annotation { "Feature Type Name" : "Feature", "Feature Type Description" : "" }
export const myFeature = defineFeature(function(context is Context, id is Id, definition is map)
    precondition{}
    {
        {
            var Q0;
            Q0=qCreatedBy(makeId("Front.planeOp"),FACE);
            var sketch = newSketch(context, id + "F0", { "sketchPlane" : qUnion([Q0])});
            skText(sketch, "E0", { "text": "Graces Medals", "fontName": "OpenSans-Bold.ttf"});
            const initialGuessF0  = {"E0": [-0.01396, 0.003, 1, 0, 0.00646]};
            skSetInitialGuess(sketch, initialGuessF0);
            skSolve(sketch);
        }
        {
            var Q0;
            Q0 = qSketchRegion(id + "F0", true);
            extrude(context, id + "F1", {"entities" : qUnion([Q0]), "depth" : 3 * mm, "offsetDistance" : 25 * mm});
        }
        {
            var Q0;
            Q0=qCreatedBy(makeId("Front.planeOp"),FACE);
            var sketch = newSketch(context, id + "F2", { "sketchPlane" : qUnion([Q0])});
            skLineSegment(sketch, "E1.bottom", {"start": v(-11.2, 3.33) * mm, "end": v(49.8, 3.33) * mm});
            skLineSegment(sketch, "E1.top", {"start": v(-11.2, 2.13) * mm, "end": v(49.8, 2.13) * mm});
            skLineSegment(sketch, "E1.left", {"start": v(-11.2, 3.33) * mm, "end": v(-11.2, 2.13) * mm});
            skLineSegment(sketch, "E1.right", {"start": v(49.8, 3.33) * mm, "end": v(49.8, 2.13) * mm});
            skSolve(sketch);
        }
        {
            var Q0;
            Q0 = qSketchRegion(id + "F2", true);
            extrude(context, id + "F3", {"entities" : qUnion([Q0]), "depth" : 4 * mm, "offsetDistance" : 25 * mm});
        }
        {
            var Q0;
            Q0=qCreatedBy(makeId("Front.planeOp"),FACE);
            var sketch = newSketch(context, id + "F4", { "sketchPlane" : qUnion([Q0])});
            skText(sketch, "E2", { "text": "Emmas Medals", "fontName": "OpenSans-Bold.ttf"});
            const initialGuessF4  = {"E2": [-0.00699, -0.01044, 1, 0, 0.00673]};
            skSetInitialGuess(sketch, initialGuessF4);
            skSolve(sketch);
        }
        {
            var Q0;
            Q0 = qSketchRegion(id + "F4", true);
            extrude(context, id + "F5", {"entities" : qUnion([Q0]), "depth" : 3 * mm, "offsetDistance" : 25 * mm});
        }
        {
            var Q0;
            Q0=qCreatedBy(makeId("Front.planeOp"),FACE);
            var sketch = newSketch(context, id + "F6", { "sketchPlane" : qUnion([Q0])});
            skLineSegment(sketch, "E3.bottom", {"start": v(-5.65, -9.96) * mm, "end": v(61.02, -9.96) * mm});
            skLineSegment(sketch, "E3.top", {"start": v(-5.65, -11.3) * mm, "end": v(61.02, -11.3) * mm});
            skLineSegment(sketch, "E3.left", {"start": v(-5.65, -9.96) * mm, "end": v(-5.65, -11.3) * mm});
            skLineSegment(sketch, "E3.right", {"start": v(61.02, -9.96) * mm, "end": v(61.02, -11.3) * mm});
            skSolve(sketch);
        }
        {
            var Q0;
            Q0 = qSketchRegion(id + "F6", true);
            extrude(context, id + "F7", {"entities" : qUnion([Q0]), "depth" : 4 * mm, "offsetDistance" : 25 * mm});
        }
        {
            var Q0;
            Q0=qCreatedBy(makeId("Front.planeOp"),FACE);
            var sketch = newSketch(context, id + "F8", { "sketchPlane" : qUnion([Q0])});
            skText(sketch, "E4", { "text": "S", "fontName": "OpenSans-Bold.ttf"});
            skText(sketch, "E5", { "text": "S", "fontName": "OpenSans-Bold.ttf"});
            const initialGuessF8  = {"E4": [-0.04804, 0.0456, 1, 0, 0.03], "E5": [0.01477, 0.04587, 1, 0, 0.02896]};
            skSetInitialGuess(sketch, initialGuessF8);
            skSolve(sketch);
        }
        {
            var Q0;
            Q0=qCreatedBy(makeId("Front.planeOp"),FACE);
            var sketch = newSketch(context, id + "F9", { "sketchPlane" : qUnion([Q0])});
            skText(sketch, "E6", { "text": "UPER", "fontName": "OpenSans-Bold.ttf"});
            const initialGuessF9  = {"E6": [-0.03335, 0.05668, 1, 0, 0.01108]};
            skSetInitialGuess(sketch, initialGuessF9);
            skSolve(sketch);
        }
        {
            var Q0;
            Q0=qCreatedBy(makeId("Front.planeOp"),FACE);
            var sketch = newSketch(context, id + "F10", { "sketchPlane" : qUnion([Q0])});
            skText(sketch, "E7", { "text": "TAR", "fontName": "OpenSans-Bold.ttf"});
            const initialGuessF10  = {"E7": [0.03342, 0.04587, 1, 0, 0.01102]};
            skSetInitialGuess(sketch, initialGuessF10);
            skSolve(sketch);
        }
        {
            var Q0;
            Q0 = qSketchRegion(id + "F10", true);
            var Q1;
            Q1 = qSketchRegion(id + "F9", true);
            var Q2;
            Q2=makeQuery(id+"F8.imprint","IMPRINT",FACE,{"disambiguationData":[TD([[makeQuery(id+"F8.imprint","IMPRINT",EDGE,{"derivedFrom":sQuery(id+"F8.wireOp",EDGE,"E4.sketch_text.stroke-0")}),-1.0]])]});
            var Q3;
            Q3=makeQuery(id+"F8.imprint","IMPRINT",FACE,{"disambiguationData":[TD([[makeQuery(id+"F8.imprint","IMPRINT",EDGE,{"derivedFrom":sQuery(id+"F8.wireOp",EDGE,"E5.sketch_text.stroke-0")}),-1.0]])]});
            extrude(context, id + "F11", {"entities" : qUnion([Q0, Q1, Q2, Q3]), "depth" : 7 * mm, "offsetDistance" : 25 * mm});
        }
        {
            var Q0;
            Q0=makeQuery(id+"F11.opExtrude","SWEPT_BODY",BODY,{"disambiguationData":[OSD([sQuery(id+"F9.wireOp",EDGE,"E6.sketch_text.stroke-15"),sQuery(id+"F9.wireOp",EDGE,"E6.sketch_text.stroke-16"),sQuery(id+"F9.wireOp",EDGE,"E6.sketch_text.stroke-17"),sQuery(id+"F9.wireOp",EDGE,"E6.sketch_text.stroke-18"),sQuery(id+"F9.wireOp",EDGE,"E6.sketch_text.stroke-19"),sQuery(id+"F9.wireOp",EDGE,"E6.sketch_text.stroke-20"),sQuery(id+"F9.wireOp",EDGE,"E6.sketch_text.stroke-21"),sQuery(id+"F9.wireOp",EDGE,"E6.sketch_text.stroke-22"),sQuery(id+"F9.wireOp",EDGE,"E6.sketch_text.stroke-23"),sQuery(id+"F9.wireOp",EDGE,"E6.sketch_text.stroke-24"),sQuery(id+"F9.wireOp",EDGE,"E6.sketch_text.stroke-25"),sQuery(id+"F9.wireOp",EDGE,"E6.sketch_text.stroke-26"),sQuery(id+"F9.wireOp",EDGE,"E6.sketch_text.stroke-27"),sQuery(id+"F9.wireOp",EDGE,"E6.sketch_text.stroke-28"),sQuery(id+"F9.wireOp",EDGE,"E6.sketch_text.stroke-29"),sQuery(id+"F9.wireOp",EDGE,"E6.sketch_text.stroke-30")])]});
            transform(context, id + "F12", {"entities" : qUnion([Q0]), "transformType" : TransformType.TRANSLATION_3D, "dx" : -2.8 * mm, "dy" : 0 * mm, "dz" : -2.3 * mm, "makeCopy" : false});
        }
        {
            var Q0;
            Q0=makeQuery(id+"F11.opExtrude","SWEPT_BODY",BODY,{"disambiguationData":[OSD([sQuery(id+"F9.wireOp",EDGE,"E6.sketch_text.stroke-31"),sQuery(id+"F9.wireOp",EDGE,"E6.sketch_text.stroke-32"),sQuery(id+"F9.wireOp",EDGE,"E6.sketch_text.stroke-33"),sQuery(id+"F9.wireOp",EDGE,"E6.sketch_text.stroke-34"),sQuery(id+"F9.wireOp",EDGE,"E6.sketch_text.stroke-35"),sQuery(id+"F9.wireOp",EDGE,"E6.sketch_text.stroke-36"),sQuery(id+"F9.wireOp",EDGE,"E6.sketch_text.stroke-37"),sQuery(id+"F9.wireOp",EDGE,"E6.sketch_text.stroke-38"),sQuery(id+"F9.wireOp",EDGE,"E6.sketch_text.stroke-39"),sQuery(id+"F9.wireOp",EDGE,"E6.sketch_text.stroke-40"),sQuery(id+"F9.wireOp",EDGE,"E6.sketch_text.stroke-41"),sQuery(id+"F9.wireOp",EDGE,"E6.sketch_text.stroke-42")])]});
            transform(context, id + "F13", {"entities" : qUnion([Q0]), "transformType" : TransformType.TRANSLATION_3D, "dx" : -5.3 * mm, "dy" : 0 * mm, "dz" : -1.2 * mm, "makeCopy" : false});
        }
        {
            var Q0;
            Q0=makeQuery(id+"F11.opExtrude","SWEPT_BODY",BODY,{"disambiguationData":[OSD([sQuery(id+"F9.wireOp",EDGE,"E6.sketch_text.stroke-43"),sQuery(id+"F9.wireOp",EDGE,"E6.sketch_text.stroke-44"),sQuery(id+"F9.wireOp",EDGE,"E6.sketch_text.stroke-45"),sQuery(id+"F9.wireOp",EDGE,"E6.sketch_text.stroke-46"),sQuery(id+"F9.wireOp",EDGE,"E6.sketch_text.stroke-47"),sQuery(id+"F9.wireOp",EDGE,"E6.sketch_text.stroke-48"),sQuery(id+"F9.wireOp",EDGE,"E6.sketch_text.stroke-49"),sQuery(id+"F9.wireOp",EDGE,"E6.sketch_text.stroke-50"),sQuery(id+"F9.wireOp",EDGE,"E6.sketch_text.stroke-51"),sQuery(id+"F9.wireOp",EDGE,"E6.sketch_text.stroke-52"),sQuery(id+"F9.wireOp",EDGE,"E6.sketch_text.stroke-53"),sQuery(id+"F9.wireOp",EDGE,"E6.sketch_text.stroke-54"),sQuery(id+"F9.wireOp",EDGE,"E6.sketch_text.stroke-55"),sQuery(id+"F9.wireOp",EDGE,"E6.sketch_text.stroke-56"),sQuery(id+"F9.wireOp",EDGE,"E6.sketch_text.stroke-57"),sQuery(id+"F9.wireOp",EDGE,"E6.sketch_text.stroke-58"),sQuery(id+"F9.wireOp",EDGE,"E6.sketch_text.stroke-59"),sQuery(id+"F9.wireOp",EDGE,"E6.sketch_text.stroke-60"),sQuery(id+"F9.wireOp",EDGE,"E6.sketch_text.stroke-61")])]});
            transform(context, id + "F14", {"entities" : qUnion([Q0]), "transformType" : TransformType.TRANSLATION_3D, "dx" : -8.5 * mm, "dy" : 0 * mm, "dz" : -4 * mm, "makeCopy" : false});
        }
        {
            var Q0;
            Q0=makeQuery(id+"F11.opExtrude","SWEPT_BODY",BODY,{"disambiguationData":[OSD([sQuery(id+"F8.wireOp",EDGE,"E5.sketch_text.stroke-0"),sQuery(id+"F8.wireOp",EDGE,"E5.sketch_text.stroke-1"),sQuery(id+"F8.wireOp",EDGE,"E5.sketch_text.stroke-2"),sQuery(id+"F8.wireOp",EDGE,"E5.sketch_text.stroke-3"),sQuery(id+"F8.wireOp",EDGE,"E5.sketch_text.stroke-4"),sQuery(id+"F8.wireOp",EDGE,"E5.sketch_text.stroke-5"),sQuery(id+"F8.wireOp",EDGE,"E5.sketch_text.stroke-6"),sQuery(id+"F8.wireOp",EDGE,"E5.sketch_text.stroke-7"),sQuery(id+"F8.wireOp",EDGE,"E5.sketch_text.stroke-8"),sQuery(id+"F8.wireOp",EDGE,"E5.sketch_text.stroke-9"),sQuery(id+"F8.wireOp",EDGE,"E5.sketch_text.stroke-10"),sQuery(id+"F8.wireOp",EDGE,"E5.sketch_text.stroke-11"),sQuery(id+"F8.wireOp",EDGE,"E5.sketch_text.stroke-12"),sQuery(id+"F8.wireOp",EDGE,"E5.sketch_text.stroke-13"),sQuery(id+"F8.wireOp",EDGE,"E5.sketch_text.stroke-14"),sQuery(id+"F8.wireOp",EDGE,"E5.sketch_text.stroke-15"),sQuery(id+"F8.wireOp",EDGE,"E5.sketch_text.stroke-16"),sQuery(id+"F8.wireOp",EDGE,"E5.sketch_text.stroke-17"),sQuery(id+"F8.wireOp",EDGE,"E5.sketch_text.stroke-18"),sQuery(id+"F8.wireOp",EDGE,"E5.sketch_text.stroke-19"),sQuery(id+"F8.wireOp",EDGE,"E5.sketch_text.stroke-20"),sQuery(id+"F8.wireOp",EDGE,"E5.sketch_text.stroke-21"),sQuery(id+"F8.wireOp",EDGE,"E5.sketch_text.stroke-22"),sQuery(id+"F8.wireOp",EDGE,"E5.sketch_text.stroke-23"),sQuery(id+"F8.wireOp",EDGE,"E5.sketch_text.stroke-24"),sQuery(id+"F8.wireOp",EDGE,"E5.sketch_text.stroke-25"),sQuery(id+"F8.wireOp",EDGE,"E5.sketch_text.stroke-26"),sQuery(id+"F8.wireOp",EDGE,"E5.sketch_text.stroke-27")])]});
            transform(context, id + "F15", {"entities" : qUnion([Q0]), "transformType" : TransformType.TRANSLATION_3D, "dx" : -21.5 * mm, "dy" : 0 * mm, "dz" : -1.5 * mm, "makeCopy" : false});
        }
        {
            var Q0;
            Q0=makeQuery(id+"F11.opExtrude","SWEPT_BODY",BODY,{"disambiguationData":[OSD([sQuery(id+"F10.wireOp",EDGE,"E7.sketch_text.stroke-0"),sQuery(id+"F10.wireOp",EDGE,"E7.sketch_text.stroke-1"),sQuery(id+"F10.wireOp",EDGE,"E7.sketch_text.stroke-2"),sQuery(id+"F10.wireOp",EDGE,"E7.sketch_text.stroke-3"),sQuery(id+"F10.wireOp",EDGE,"E7.sketch_text.stroke-4"),sQuery(id+"F10.wireOp",EDGE,"E7.sketch_text.stroke-5"),sQuery(id+"F10.wireOp",EDGE,"E7.sketch_text.stroke-6"),sQuery(id+"F10.wireOp",EDGE,"E7.sketch_text.stroke-7")])]});
            transform(context, id + "F16", {"entities" : qUnion([Q0]), "transformType" : TransformType.TRANSLATION_3D, "dx" : -21.7 * mm, "dy" : 0 * mm, "dz" : -0.7 * mm, "makeCopy" : false});
        }
        {
            var Q0;
            Q0=makeQuery(id+"F11.opExtrude","SWEPT_BODY",BODY,{"disambiguationData":[OSD([sQuery(id+"F10.wireOp",EDGE,"E7.sketch_text.stroke-8"),sQuery(id+"F10.wireOp",EDGE,"E7.sketch_text.stroke-9"),sQuery(id+"F10.wireOp",EDGE,"E7.sketch_text.stroke-10"),sQuery(id+"F10.wireOp",EDGE,"E7.sketch_text.stroke-11"),sQuery(id+"F10.wireOp",EDGE,"E7.sketch_text.stroke-12"),sQuery(id+"F10.wireOp",EDGE,"E7.sketch_text.stroke-13"),sQuery(id+"F10.wireOp",EDGE,"E7.sketch_text.stroke-14"),sQuery(id+"F10.wireOp",EDGE,"E7.sketch_text.stroke-15"),sQuery(id+"F10.wireOp",EDGE,"E7.sketch_text.stroke-16"),sQuery(id+"F10.wireOp",EDGE,"E7.sketch_text.stroke-17"),sQuery(id+"F10.wireOp",EDGE,"E7.sketch_text.stroke-18"),sQuery(id+"F10.wireOp",EDGE,"E7.sketch_text.stroke-19")])]});
            transform(context, id + "F17", {"entities" : qUnion([Q0]), "transformType" : TransformType.TRANSLATION_3D, "dx" : -25.6 * mm, "dy" : 0 * mm, "dz" : 1.9 * mm, "makeCopy" : false});
        }
        {
            var Q0;
            Q0=makeQuery(id+"F11.opExtrude","SWEPT_BODY",BODY,{"disambiguationData":[OSD([sQuery(id+"F10.wireOp",EDGE,"E7.sketch_text.stroke-20"),sQuery(id+"F10.wireOp",EDGE,"E7.sketch_text.stroke-21"),sQuery(id+"F10.wireOp",EDGE,"E7.sketch_text.stroke-22"),sQuery(id+"F10.wireOp",EDGE,"E7.sketch_text.stroke-23"),sQuery(id+"F10.wireOp",EDGE,"E7.sketch_text.stroke-24"),sQuery(id+"F10.wireOp",EDGE,"E7.sketch_text.stroke-25"),sQuery(id+"F10.wireOp",EDGE,"E7.sketch_text.stroke-26"),sQuery(id+"F10.wireOp",EDGE,"E7.sketch_text.stroke-27"),sQuery(id+"F10.wireOp",EDGE,"E7.sketch_text.stroke-28"),sQuery(id+"F10.wireOp",EDGE,"E7.sketch_text.stroke-29"),sQuery(id+"F10.wireOp",EDGE,"E7.sketch_text.stroke-30"),sQuery(id+"F10.wireOp",EDGE,"E7.sketch_text.stroke-31"),sQuery(id+"F10.wireOp",EDGE,"E7.sketch_text.stroke-32"),sQuery(id+"F10.wireOp",EDGE,"E7.sketch_text.stroke-33"),sQuery(id+"F10.wireOp",EDGE,"E7.sketch_text.stroke-34"),sQuery(id+"F10.wireOp",EDGE,"E7.sketch_text.stroke-35"),sQuery(id+"F10.wireOp",EDGE,"E7.sketch_text.stroke-36"),sQuery(id+"F10.wireOp",EDGE,"E7.sketch_text.stroke-37"),sQuery(id+"F10.wireOp",EDGE,"E7.sketch_text.stroke-38")])]});
            transform(context, id + "F18", {"entities" : qUnion([Q0]), "transformType" : TransformType.TRANSLATION_3D, "dx" : -28.4 * mm, "dy" : 0 * mm, "dz" : -0.5 * mm, "makeCopy" : false});
        }
        {
            var Q0;
            Q0=qCreatedBy(makeId("Front.planeOp"),FACE);
            var sketch = newSketch(context, id + "F19", { "sketchPlane" : qUnion([Q0])});
            skLineSegment(sketch, "E8", {"start": v(62.77, 66.37) * mm, "end": v(70.1, 78.5) * mm});
            skLineSegment(sketch, "E9", {"start": v(70.1, 78.5) * mm, "end": v(72.24, 66.28) * mm});
            skLineSegment(sketch, "E10", {"start": v(72.24, 66.28) * mm, "end": v(86.36, 63.38) * mm});
            skLineSegment(sketch, "E11", {"start": v(86.36, 63.38) * mm, "end": v(73.94, 57.58) * mm});
            skLineSegment(sketch, "E12", {"start": v(73.94, 57.58) * mm, "end": v(79.41, 48.25) * mm});
            skLineSegment(sketch, "E13", {"start": v(79.41, 48.25) * mm, "end": v(66.79, 53.47) * mm});
            skLineSegment(sketch, "E14", {"start": v(66.79, 53.47) * mm, "end": v(57.96, 45.15) * mm});
            skLineSegment(sketch, "E15", {"start": v(57.96, 45.15) * mm, "end": v(61.18, 58.45) * mm});
            skLineSegment(sketch, "E16", {"start": v(61.18, 58.45) * mm, "end": v(50.5, 63.97) * mm});
            skLineSegment(sketch, "E17", {"start": v(50.5, 63.97) * mm, "end": v(62.77, 66.37) * mm});
            skSolve(sketch);
        }
        {
            var Q0;
            Q0 = qSketchRegion(id + "F19", true);
            extrude(context, id + "F20", {"entities" : qUnion([Q0]), "depth" : 3 * mm, "offsetDistance" : 25 * mm});
        }
        {
            var Q0;
            Q0=makeQuery(id+"F20.opExtrude","SWEPT_BODY",BODY,{"disambiguationData":[OSD([sQuery(id+"F19.wireOp",EDGE,"E8"),sQuery(id+"F19.wireOp",EDGE,"E9"),sQuery(id+"F19.wireOp",EDGE,"E10"),sQuery(id+"F19.wireOp",EDGE,"E11"),sQuery(id+"F19.wireOp",EDGE,"E12"),sQuery(id+"F19.wireOp",EDGE,"E13"),sQuery(id+"F19.wireOp",EDGE,"E14"),sQuery(id+"F19.wireOp",EDGE,"E15"),sQuery(id+"F19.wireOp",EDGE,"E16"),sQuery(id+"F19.wireOp",EDGE,"E17")])]});
            transform(context, id + "F21", {"entities" : qUnion([Q0]), "transformType" : TransformType.TRANSLATION_3D, "dx" : -83.4 * mm, "dy" : 0 * mm, "dz" : 5.9 * mm, "makeCopy" : false});
        }
        {
            var Q0;
            Q0=makeQuery(id+"F20.opExtrude","SWEPT_BODY",BODY,{"disambiguationData":[OSD([sQuery(id+"F19.wireOp",EDGE,"E8"),sQuery(id+"F19.wireOp",EDGE,"E9"),sQuery(id+"F19.wireOp",EDGE,"E10"),sQuery(id+"F19.wireOp",EDGE,"E11"),sQuery(id+"F19.wireOp",EDGE,"E12"),sQuery(id+"F19.wireOp",EDGE,"E13"),sQuery(id+"F19.wireOp",EDGE,"E14"),sQuery(id+"F19.wireOp",EDGE,"E15"),sQuery(id+"F19.wireOp",EDGE,"E16"),sQuery(id+"F19.wireOp",EDGE,"E17")])]});
            transform(context, id + "F22", {"entities" : qUnion([Q0]), "transformType" : TransformType.TRANSLATION_3D, "dx" : 38.7 * mm, "dy" : 0 * mm, "dz" : -7.2 * mm, "makeCopy" : true});
        }
        {
            var Q0;
            Q0=makeQuery(id+"F22.opPattern","COPY",BODY,{"derivedFrom":makeQuery(id+"F20.opExtrude","SWEPT_BODY",BODY,{"disambiguationData":[OSD([sQuery(id+"F19.wireOp",EDGE,"E8"),sQuery(id+"F19.wireOp",EDGE,"E9"),sQuery(id+"F19.wireOp",EDGE,"E10"),sQuery(id+"F19.wireOp",EDGE,"E11"),sQuery(id+"F19.wireOp",EDGE,"E12"),sQuery(id+"F19.wireOp",EDGE,"E13"),sQuery(id+"F19.wireOp",EDGE,"E14"),sQuery(id+"F19.wireOp",EDGE,"E15"),sQuery(id+"F19.wireOp",EDGE,"E16"),sQuery(id+"F19.wireOp",EDGE,"E17")])]}),"instanceName":"1"});
            var Q1;
            Q1=makeQuery(id+"F11.opExtrude","SWEPT_EDGE",EDGE,{"disambiguationData":[OSD([sQuery(id+"F10.wireOp",EDGE,"E7.sketch_text.stroke-13"),sQuery(id+"F10.wireOp",EDGE,"E7.sketch_text.stroke-14")])]});
            transform(context, id + "F23", {"entities" : qUnion([Q0]), "transformType" : TransformType.ROTATION, "transformAxis" : qUnion([Q1]), "angle" : 45 * degree, "makeCopy" : false});
        }
        {
            var Q0;
            Q0=makeQuery(id+"F11.opExtrude","CAP_FACE",FACE,{"disambiguationData":[OSD([sQuery(id+"F9.wireOp",EDGE,"E6.sketch_text.stroke-0"),sQuery(id+"F9.wireOp",EDGE,"E6.sketch_text.stroke-1"),sQuery(id+"F9.wireOp",EDGE,"E6.sketch_text.stroke-2"),sQuery(id+"F9.wireOp",EDGE,"E6.sketch_text.stroke-3"),sQuery(id+"F9.wireOp",EDGE,"E6.sketch_text.stroke-4"),sQuery(id+"F9.wireOp",EDGE,"E6.sketch_text.stroke-5"),sQuery(id+"F9.wireOp",EDGE,"E6.sketch_text.stroke-6"),sQuery(id+"F9.wireOp",EDGE,"E6.sketch_text.stroke-7"),sQuery(id+"F9.wireOp",EDGE,"E6.sketch_text.stroke-8"),sQuery(id+"F9.wireOp",EDGE,"E6.sketch_text.stroke-9"),sQuery(id+"F9.wireOp",EDGE,"E6.sketch_text.stroke-10"),sQuery(id+"F9.wireOp",EDGE,"E6.sketch_text.stroke-11"),sQuery(id+"F9.wireOp",EDGE,"E6.sketch_text.stroke-12"),sQuery(id+"F9.wireOp",EDGE,"E6.sketch_text.stroke-13"),sQuery(id+"F9.wireOp",EDGE,"E6.sketch_text.stroke-14")])],"isStart":false});
            extrude(context, id + "F24", {"entities" : qUnion([Q0]), "depth" : 1 * mm, "offsetDistance" : 25 * mm});
        }
        {
            var Q0;
            Q0=makeQuery(id+"F11.opExtrude","CAP_FACE",FACE,{"disambiguationData":[OSD([sQuery(id+"F9.wireOp",EDGE,"E6.sketch_text.stroke-31"),sQuery(id+"F9.wireOp",EDGE,"E6.sketch_text.stroke-32"),sQuery(id+"F9.wireOp",EDGE,"E6.sketch_text.stroke-33"),sQuery(id+"F9.wireOp",EDGE,"E6.sketch_text.stroke-34"),sQuery(id+"F9.wireOp",EDGE,"E6.sketch_text.stroke-35"),sQuery(id+"F9.wireOp",EDGE,"E6.sketch_text.stroke-36"),sQuery(id+"F9.wireOp",EDGE,"E6.sketch_text.stroke-37"),sQuery(id+"F9.wireOp",EDGE,"E6.sketch_text.stroke-38"),sQuery(id+"F9.wireOp",EDGE,"E6.sketch_text.stroke-39"),sQuery(id+"F9.wireOp",EDGE,"E6.sketch_text.stroke-40"),sQuery(id+"F9.wireOp",EDGE,"E6.sketch_text.stroke-41"),sQuery(id+"F9.wireOp",EDGE,"E6.sketch_text.stroke-42")])],"isStart":false});
            extrude(context, id + "F25", {"entities" : qUnion([Q0]), "operationType" : NewBodyOperationType.REMOVE, "oppositeDirection" : true, "depth" : 1 * mm, "offsetDistance" : 25 * mm});
        }
        {
            var Q0;
            Q0=makeQuery(id+"F11.opExtrude","CAP_FACE",FACE,{"disambiguationData":[OSD([sQuery(id+"F9.wireOp",EDGE,"E6.sketch_text.stroke-43"),sQuery(id+"F9.wireOp",EDGE,"E6.sketch_text.stroke-44"),sQuery(id+"F9.wireOp",EDGE,"E6.sketch_text.stroke-45"),sQuery(id+"F9.wireOp",EDGE,"E6.sketch_text.stroke-46"),sQuery(id+"F9.wireOp",EDGE,"E6.sketch_text.stroke-47"),sQuery(id+"F9.wireOp",EDGE,"E6.sketch_text.stroke-48"),sQuery(id+"F9.wireOp",EDGE,"E6.sketch_text.stroke-49"),sQuery(id+"F9.wireOp",EDGE,"E6.sketch_text.stroke-50"),sQuery(id+"F9.wireOp",EDGE,"E6.sketch_text.stroke-51"),sQuery(id+"F9.wireOp",EDGE,"E6.sketch_text.stroke-52"),sQuery(id+"F9.wireOp",EDGE,"E6.sketch_text.stroke-53"),sQuery(id+"F9.wireOp",EDGE,"E6.sketch_text.stroke-54"),sQuery(id+"F9.wireOp",EDGE,"E6.sketch_text.stroke-55"),sQuery(id+"F9.wireOp",EDGE,"E6.sketch_text.stroke-56"),sQuery(id+"F9.wireOp",EDGE,"E6.sketch_text.stroke-57"),sQuery(id+"F9.wireOp",EDGE,"E6.sketch_text.stroke-58"),sQuery(id+"F9.wireOp",EDGE,"E6.sketch_text.stroke-59"),sQuery(id+"F9.wireOp",EDGE,"E6.sketch_text.stroke-60"),sQuery(id+"F9.wireOp",EDGE,"E6.sketch_text.stroke-61")])],"isStart":false});
            extrude(context, id + "F26", {"entities" : qUnion([Q0]), "depth" : 1.5 * mm, "offsetDistance" : 25 * mm});
        }
        {
            var Q0;
            Q0=makeQuery(id+"F11.opExtrude","CAP_FACE",FACE,{"disambiguationData":[OSD([sQuery(id+"F10.wireOp",EDGE,"E7.sketch_text.stroke-0"),sQuery(id+"F10.wireOp",EDGE,"E7.sketch_text.stroke-1"),sQuery(id+"F10.wireOp",EDGE,"E7.sketch_text.stroke-2"),sQuery(id+"F10.wireOp",EDGE,"E7.sketch_text.stroke-3"),sQuery(id+"F10.wireOp",EDGE,"E7.sketch_text.stroke-4"),sQuery(id+"F10.wireOp",EDGE,"E7.sketch_text.stroke-5"),sQuery(id+"F10.wireOp",EDGE,"E7.sketch_text.stroke-6"),sQuery(id+"F10.wireOp",EDGE,"E7.sketch_text.stroke-7")])],"isStart":false});
            extrude(context, id + "F27", {"entities" : qUnion([Q0]), "depth" : 1.5 * mm, "offsetDistance" : 25 * mm});
        }
        {
            var Q0;
            Q0=makeQuery(id+"F11.opExtrude","CAP_FACE",FACE,{"disambiguationData":[OSD([sQuery(id+"F10.wireOp",EDGE,"E7.sketch_text.stroke-20"),sQuery(id+"F10.wireOp",EDGE,"E7.sketch_text.stroke-21"),sQuery(id+"F10.wireOp",EDGE,"E7.sketch_text.stroke-22"),sQuery(id+"F10.wireOp",EDGE,"E7.sketch_text.stroke-23"),sQuery(id+"F10.wireOp",EDGE,"E7.sketch_text.stroke-24"),sQuery(id+"F10.wireOp",EDGE,"E7.sketch_text.stroke-25"),sQuery(id+"F10.wireOp",EDGE,"E7.sketch_text.stroke-26"),sQuery(id+"F10.wireOp",EDGE,"E7.sketch_text.stroke-27"),sQuery(id+"F10.wireOp",EDGE,"E7.sketch_text.stroke-28"),sQuery(id+"F10.wireOp",EDGE,"E7.sketch_text.stroke-29"),sQuery(id+"F10.wireOp",EDGE,"E7.sketch_text.stroke-30"),sQuery(id+"F10.wireOp",EDGE,"E7.sketch_text.stroke-31"),sQuery(id+"F10.wireOp",EDGE,"E7.sketch_text.stroke-32"),sQuery(id+"F10.wireOp",EDGE,"E7.sketch_text.stroke-33"),sQuery(id+"F10.wireOp",EDGE,"E7.sketch_text.stroke-34"),sQuery(id+"F10.wireOp",EDGE,"E7.sketch_text.stroke-35"),sQuery(id+"F10.wireOp",EDGE,"E7.sketch_text.stroke-36"),sQuery(id+"F10.wireOp",EDGE,"E7.sketch_text.stroke-37"),sQuery(id+"F10.wireOp",EDGE,"E7.sketch_text.stroke-38")])],"isStart":false});
            extrude(context, id + "F28", {"entities" : qUnion([Q0]), "operationType" : NewBodyOperationType.REMOVE, "oppositeDirection" : true, "depth" : 1.5 * mm, "offsetDistance" : 25 * mm});
        }
        {
            var Q0;
            Q0=qCreatedBy(makeId("Front.planeOp"),FACE);
            var sketch = newSketch(context, id + "F29", { "sketchPlane" : qUnion([Q0])});
            skLineSegment(sketch, "E18.bottom", {"start": v(-74.47, 45.8) * mm, "end": v(65.23, 45.8) * mm});
            skLineSegment(sketch, "E18.top", {"start": v(-74.47, 42.06) * mm, "end": v(65.23, 42.06) * mm});
            skLineSegment(sketch, "E18.left", {"start": v(-74.47, 45.8) * mm, "end": v(-74.47, 42.06) * mm});
            skLineSegment(sketch, "E18.right", {"start": v(65.23, 45.8) * mm, "end": v(65.23, 42.06) * mm});
            skSolve(sketch);
        }
        {
            var Q0;
            Q0 = qSketchRegion(id + "F29", true);
            extrude(context, id + "F30", {"entities" : qUnion([Q0]), "depth" : 9.7 * mm, "offsetDistance" : 25 * mm});
        }
        {
            var Q0;
            Q0=makeQuery(id+"F30.opExtrude","CAP_EDGE",EDGE,{"disambiguationData":[OSD([sQuery(id+"F29.wireOp",EDGE,"E18.top")])],"isStart":false});
            chamfer(context, id + "F31", {"entities" : qUnion([Q0]), "width" : 4.7 * mm, "tangentPropagation" : true});
        }
    });